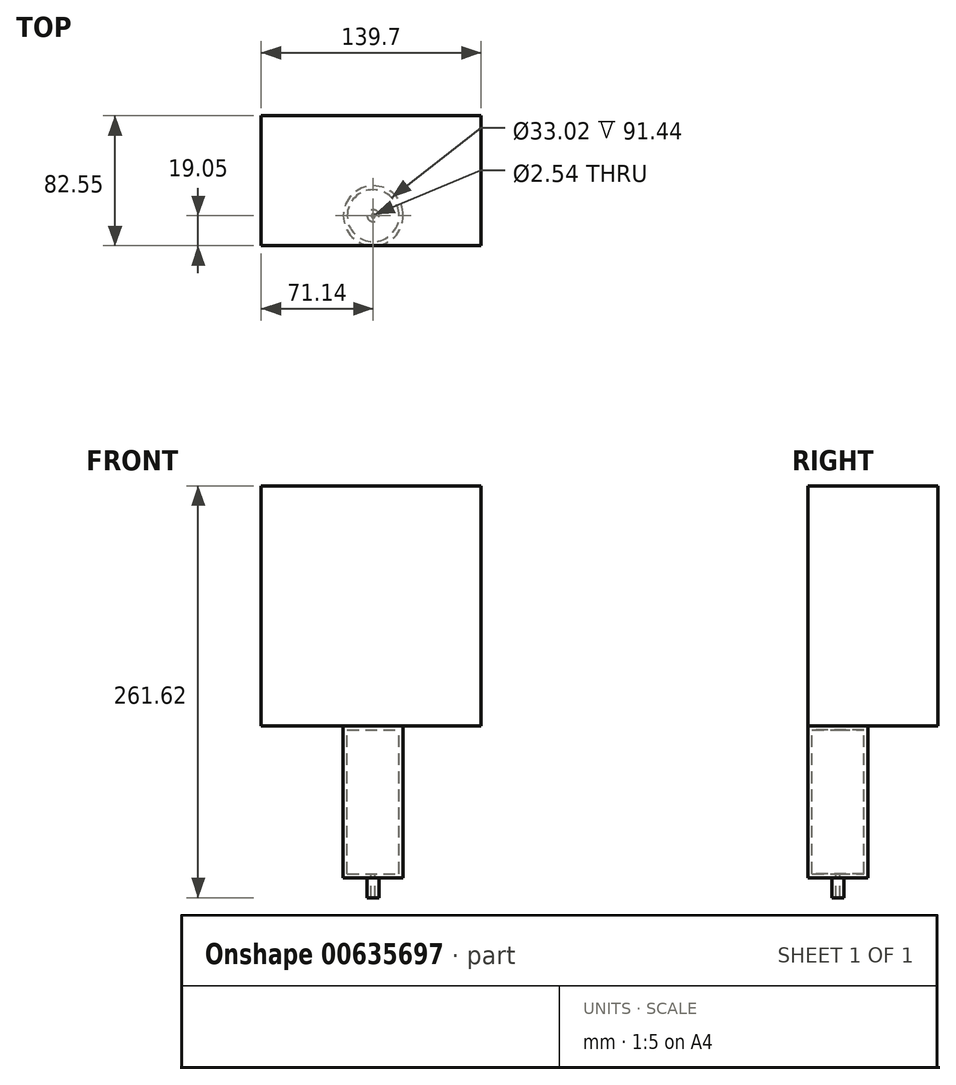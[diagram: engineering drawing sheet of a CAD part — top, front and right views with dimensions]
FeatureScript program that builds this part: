
annotation { "Feature Type Name" : "Feature", "Feature Type Description" : "" }
export const myFeature = defineFeature(function(context is Context, id is Id, definition is map)
    precondition{}
    {
        {
            var Q0;
            Q0=qCreatedBy(makeId("Front.planeOp"),FACE);
            var sketch = newSketch(context, id + "F0", { "sketchPlane" : qUnion([Q0])});
            skLineSegment(sketch, "E0.bottom", {"start": v(-71.14, 93.58) * mm, "end": v(68.56, 93.58) * mm});
            skLineSegment(sketch, "E0.top", {"start": v(-71.14, -58.82) * mm, "end": v(68.56, -58.82) * mm});
            skLineSegment(sketch, "E0.left", {"start": v(-71.14, 93.58) * mm, "end": v(-71.14, -58.82) * mm});
            skLineSegment(sketch, "E0.right", {"start": v(68.56, 93.58) * mm, "end": v(68.56, -58.82) * mm});
            skSolve(sketch);
        }
        {
            var Q0;
            Q0 = qSketchRegion(id + "F0", true);
            extrude(context, id + "F1", {"entities" : qUnion([Q0]), "oppositeDirection" : true, "depth" : 82.55 * mm, "offsetDistance" : 25.4 * mm});
        }
        {
            var Q0;
            Q0=makeQuery(id+"F1.opExtrude","SWEPT_FACE",FACE,{"disambiguationData":[OSD([sQuery(id+"F0.wireOp",EDGE,"E0.top")])]});
            var sketch = newSketch(context, id + "F2", { "sketchPlane" : qUnion([Q0])});
            skLineSegment(sketch, "E1", {"start": v(0, 0) * mm, "end": v(-19.05, 0) * mm, "construction": true});
            skLineSegment(sketch, "E2", {"start": v(0, 0) * mm, "end": v(19.05, 0) * mm, "construction": true});
            skLineSegment(sketch, "E3", {"start": v(0, 0) * mm, "end": v(0, -19.05) * mm, "construction": true});
            skCircle(sketch, "E4", {"center": v(0, -19.05) * mm, "radius": 19.05 * mm});
            skSolve(sketch);
        }
        {
            var Q0;
            Q0 = qSketchRegion(id + "F2", true);
            extrude(context, id + "F3", {"entities" : qUnion([Q0]), "depth" : 96.52 * mm, "offsetDistance" : 25.4 * mm});
        }
        {
            var Q0;
            Q0=makeQuery(id+"F3.opExtrude","CAP_FACE",FACE,{"disambiguationData":[OSD([sQuery(id+"F2.wireOp",EDGE,"E4")])],"isStart":false});
            var sketch = newSketch(context, id + "F4", { "sketchPlane" : qUnion([Q0])});
            skCircle(sketch, "E5", {"center": v(0, -19.05) * mm, "radius": 3.81 * mm});
            skSolve(sketch);
        }
        {
            var Q0;
            Q0=makeQuery(id+"F4.imprint","IMPRINT",FACE,{"disambiguationData":[TD([[makeQuery(id+"F4.imprint","IMPRINT",EDGE,{"derivedFrom":sQuery(id+"F4.wireOp",EDGE,"E5")}),1.0]])]});
            extrude(context, id + "F5", {"entities" : qUnion([Q0]), "operationType" : NewBodyOperationType.ADD, "depth" : 12.7 * mm, "offsetDistance" : 25.4 * mm});
        }
        {
            var Q0;
            Q0=makeQuery(id+"F5.opExtrude","CAP_FACE",FACE,{"disambiguationData":[OSD([sQuery(id+"F4.wireOp",EDGE,"E5")])],"isStart":false});
            shell(context, id + "F6", {"entities" : qUnion([Q0]), "thickness" : 2.54 * mm});
        }
    });
